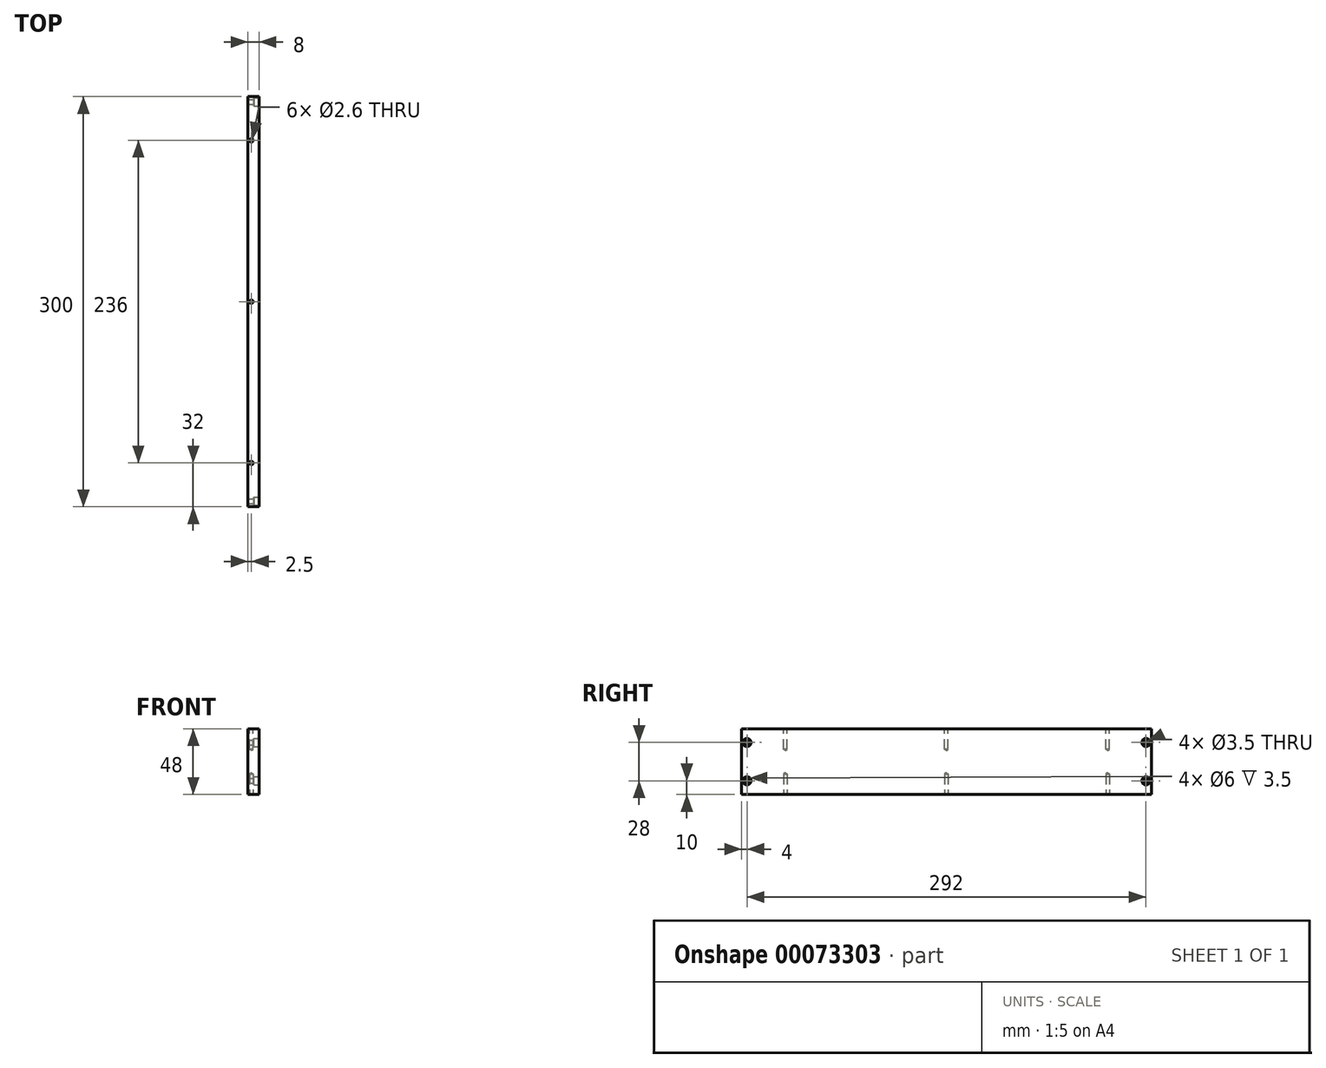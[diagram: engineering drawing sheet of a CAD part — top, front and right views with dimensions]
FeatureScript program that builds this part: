
annotation { "Feature Type Name" : "Feature", "Feature Type Description" : "" }
export const myFeature = defineFeature(function(context is Context, id is Id, definition is map)
    precondition{}
    {
        {
            var Q0;
            Q0=qCreatedBy(makeId("Front.planeOp"),FACE);
            var sketch = newSketch(context, id + "F0", { "sketchPlane" : qUnion([Q0])});
            skLineSegment(sketch, "E0.rect.bottom", {"start": v(-4, 24) * mm, "end": v(4, 24) * mm});
            skLineSegment(sketch, "E0.rect.top", {"start": v(-4, -24) * mm, "end": v(4, -24) * mm});
            skLineSegment(sketch, "E0.rect.left", {"start": v(-4, 24) * mm, "end": v(-4, -24) * mm});
            skLineSegment(sketch, "E0.rect.right", {"start": v(4, 24) * mm, "end": v(4, -24) * mm});
            skPoint(sketch, "E0.rect.middle", {"position": v(0, 0) * mm});
            skSolve(sketch);
        }
        {
            var Q0;
            Q0=makeQuery(id+"F0.imprint","IMPRINT",FACE,{"disambiguationData":[TD([[makeQuery(id+"F0.imprint","IMPRINT",EDGE,{"derivedFrom":sQuery(id+"F0.wireOp",EDGE,"E0.rect.bottom")}),-1.0]])]});
            extrude(context, id + "F1", {"entities" : qUnion([Q0]), "endBound" : BoundingType.SYMMETRIC, "depth" : 300 * mm});
        }
        {
            var Q0;
            Q0=makeQuery(id+"F1.opExtrude","SWEPT_FACE",FACE,{"disambiguationData":[OSD([sQuery(id+"F0.wireOp",EDGE,"E0.rect.right")])]});
            var sketch = newSketch(context, id + "F2", { "sketchPlane" : qUnion([Q0])});
            skPoint(sketch, "E1", {"position": v(-146, 14) * mm});
            skPoint(sketch, "E2.MirrorP", {"position": v(146, 14) * mm});
            skPoint(sketch, "E3.MirrorP", {"position": v(-146, -14) * mm});
            skPoint(sketch, "E4.MirrorP", {"position": v(146, -14) * mm});
            skSolve(sketch);
        }
        {
            var Q0;
            Q0=makeQuery(id+"F1.opExtrude","SWEPT_FACE",FACE,{"disambiguationData":[OSD([sQuery(id+"F0.wireOp",EDGE,"E0.rect.bottom")])]});
            var sketch = newSketch(context, id + "F3", { "sketchPlane" : qUnion([Q0])});
            skPoint(sketch, "E5", {"position": v(-1.5, -118) * mm});
            skPoint(sketch, "E6", {"position": v(-1.5, 0) * mm});
            skPoint(sketch, "E7", {"position": v(-1.5, 118) * mm});
            skSolve(sketch);
        }
        {
            var Q0;
            Q0=makeQuery(id+"F1.opExtrude","SWEPT_FACE",FACE,{"disambiguationData":[OSD([sQuery(id+"F0.wireOp",EDGE,"E0.rect.top")])]});
            var sketch = newSketch(context, id + "F4", { "sketchPlane" : qUnion([Q0])});
            skPoint(sketch, "E8", {"position": v(-1.5, 118) * mm});
            skPoint(sketch, "E9", {"position": v(0, 118) * mm});
            skPoint(sketch, "E10", {"position": v(-1.5, 0) * mm});
            skPoint(sketch, "E11", {"position": v(-1.5, -118) * mm});
            skSolve(sketch);
        }
        {
            var Q0;
            Q0=sQuery(id+"F3.wireOp",VERTEX,"E5");
            var Q1;
            Q1=sQuery(id+"F3.wireOp",VERTEX,"E6");
            var Q2;
            Q2=sQuery(id+"F3.wireOp",VERTEX,"E7");
            var Q3;
            Q3=sQuery(id+"F4.wireOp",VERTEX,"E8");
            var Q4;
            Q4=sQuery(id+"F4.wireOp",VERTEX,"E10");
            var Q5;
            Q5=sQuery(id+"F4.wireOp",VERTEX,"E11");
            var Q6;
            Q6=makeQuery(id+"F1.opExtrude","SWEPT_BODY",BODY,{"disambiguationData":[OSD([sQuery(id+"F0.wireOp",EDGE,"E0.rect.bottom"),sQuery(id+"F0.wireOp",EDGE,"E0.rect.top"),sQuery(id+"F0.wireOp",EDGE,"E0.rect.left"),sQuery(id+"F0.wireOp",EDGE,"E0.rect.right")])]});
            hole(context, id + "F5", {"style" : HoleStyle.SIMPLE, "holeDiameter" : 2.6 * mm, "endStyle" : HoleEndStyle.BLIND, "holeDepth" : 15 * mm, "locations" : qUnion([Q0, Q1, Q2, Q3, Q4, Q5]), "scope" : qUnion([Q6]), "tappedDepth" : 12 * mm, "tapClearance" : 3});
        }
        {
            var Q0;
            Q0=sQuery(id+"F2.wireOp",VERTEX,"E1");
            var Q1;
            Q1=sQuery(id+"F2.wireOp",VERTEX,"E3.MirrorP");
            var Q2;
            Q2=sQuery(id+"F2.wireOp",VERTEX,"E2.MirrorP");
            var Q3;
            Q3=sQuery(id+"F2.wireOp",VERTEX,"E4.MirrorP");
            var Q4;
            Q4=makeQuery(id+"F1.opExtrude","SWEPT_BODY",BODY,{"disambiguationData":[OSD([sQuery(id+"F0.wireOp",EDGE,"E0.rect.bottom"),sQuery(id+"F0.wireOp",EDGE,"E0.rect.top"),sQuery(id+"F0.wireOp",EDGE,"E0.rect.left"),sQuery(id+"F0.wireOp",EDGE,"E0.rect.right")])]});
            hole(context, id + "F6", {"style" : HoleStyle.C_BORE, "holeDiameter" : 3.5 * mm, "cBoreDiameter" : 6 * mm, "cBoreDepth" : 3.5 * mm, "endStyle" : HoleEndStyle.THROUGH, "locations" : qUnion([Q0, Q1, Q2, Q3]), "scope" : qUnion([Q4]), "tappedDepth" : 12 * mm, "tapClearance" : 3});
        }
    });
